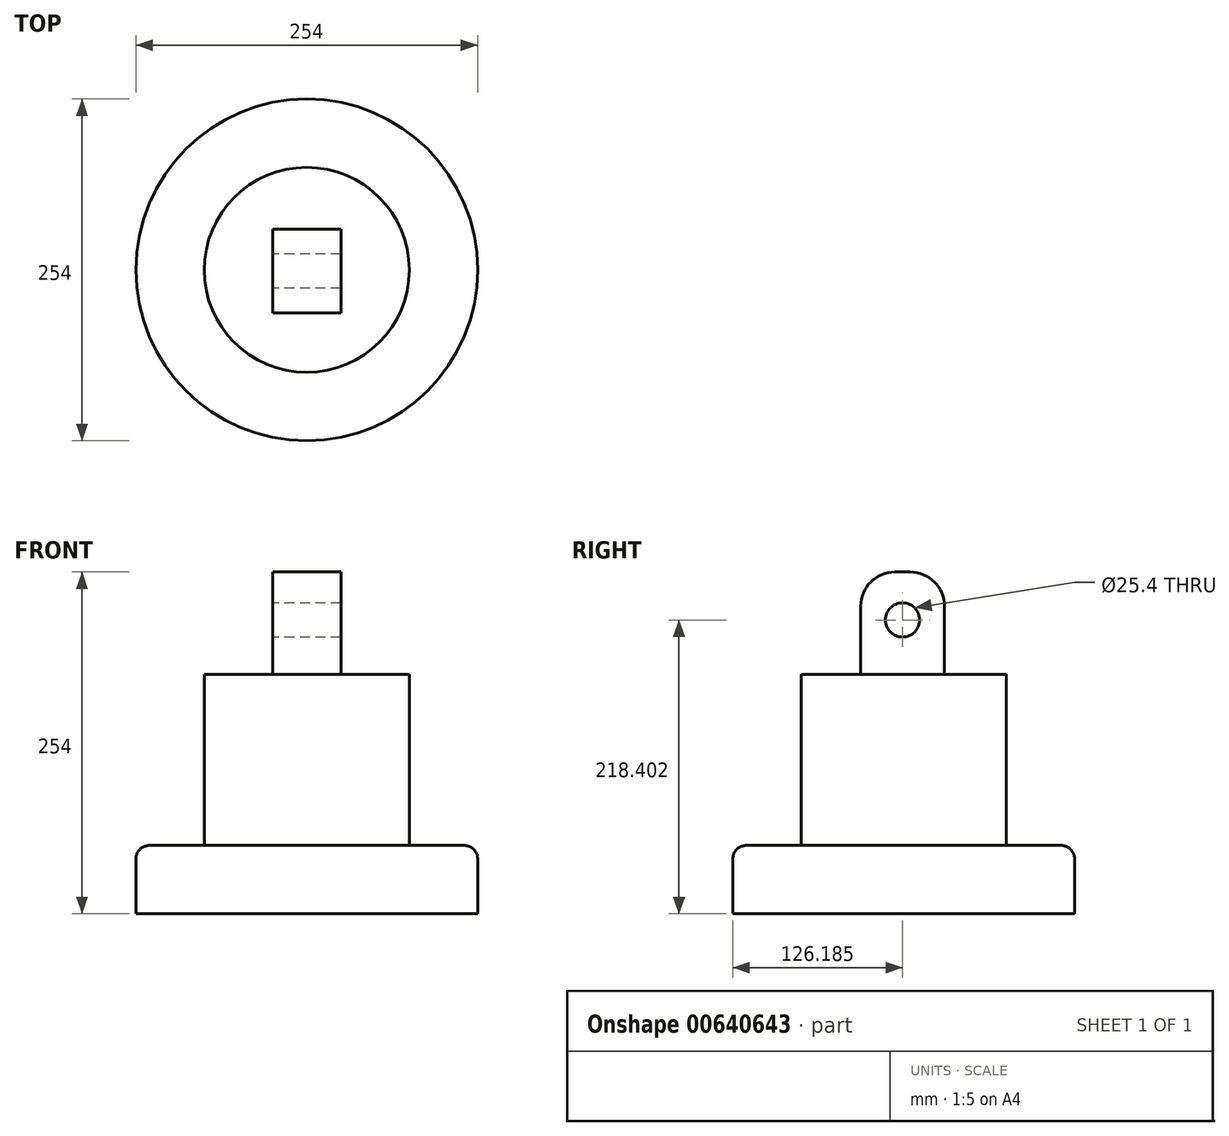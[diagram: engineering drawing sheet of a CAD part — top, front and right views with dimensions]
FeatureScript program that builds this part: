
annotation { "Feature Type Name" : "Feature", "Feature Type Description" : "" }
export const myFeature = defineFeature(function(context is Context, id is Id, definition is map)
    precondition{}
    {
        {
            var Q0;
            Q0=qCreatedBy(makeId("Front.planeOp"),FACE);
            var sketch = newSketch(context, id + "F0", { "sketchPlane" : qUnion([Q0])});
            skLineSegment(sketch, "E0", {"start": v(-155.87, 46) * mm, "end": v(-155.87, -4.8) * mm});
            skLineSegment(sketch, "E1", {"start": v(-155.87, -4.8) * mm, "end": v(-28.87, -4.8) * mm});
            skLineSegment(sketch, "E2", {"start": v(-28.87, -4.8) * mm, "end": v(-28.87, 46) * mm});
            skLineSegment(sketch, "E3", {"start": v(-28.87, 46) * mm, "end": v(-155.87, 46) * mm});
            skSolve(sketch);
        }
        {
            var Q0;
            Q0=makeQuery(id+"F0.imprint","IMPRINT",FACE,{"disambiguationData":[TD([[makeQuery(id+"F0.imprint","IMPRINT",EDGE,{"derivedFrom":sQuery(id+"F0.wireOp",EDGE,"E0")}),1.0]])]});
            var Q1;
            Q1=sQuery(id+"F0.wireOp",EDGE,"E0");
            revolve(context, id + "F1", {"entities" : qUnion([Q0]), "axis" : qUnion([Q1]), "revolveType" : RevolveType.FULL});
        }
        {
            var Q0;
            Q0=makeQuery(id+"F1.opRevolve","SWEPT_FACE",FACE,{"disambiguationData":[OSD([sQuery(id+"F0.wireOp",EDGE,"E3")])]});
            var sketch = newSketch(context, id + "F2", { "sketchPlane" : qUnion([Q0])});
            skCircle(sketch, "E4", {"center": v(-155.87, 0) * mm, "radius": 76.2 * mm});
            skSolve(sketch);
        }
        {
            var Q0;
            Q0=qSketchRegion(id+"F2",true);
            extrude(context, id + "F3", {"entities" : qUnion([Q0]), "operationType" : NewBodyOperationType.ADD, "depth" : 127 * mm});
        }
        {
            var Q0;
            Q0=makeQuery(id+"F3.opExtrude","CAP_FACE",FACE,{"disambiguationData":[OSD([sQuery(id+"F2.wireOp",EDGE,"E4")])],"isStart":false});
            var sketch = newSketch(context, id + "F4", { "sketchPlane" : qUnion([Q0])});
            skLineSegment(sketch, "E5", {"start": v(-155.87, 30.3) * mm, "end": v(-130.47, 30.3) * mm});
            skLineSegment(sketch, "E6", {"start": v(-130.47, 30.3) * mm, "end": v(-130.47, -31.94) * mm});
            skLineSegment(sketch, "E7", {"start": v(-130.47, -31.94) * mm, "end": v(-155.87, -31.94) * mm});
            skLineSegment(sketch, "E8", {"start": v(-155.87, 30.3) * mm, "end": v(-181.27, 30.3) * mm});
            skLineSegment(sketch, "E9", {"start": v(-181.27, 30.3) * mm, "end": v(-181.27, -31.94) * mm});
            skLineSegment(sketch, "E10", {"start": v(-181.27, -31.94) * mm, "end": v(-155.87, -31.94) * mm});
            skPoint(sketch, "E11.start.orphan", {"position": v(-155.87, 0) * mm});
            skSolve(sketch);
        }
        {
            var Q0;
            Q0=makeQuery(id+"F4.imprint","IMPRINT",FACE,{"disambiguationData":[TD([[makeQuery(id+"F4.imprint","IMPRINT",EDGE,{"derivedFrom":sQuery(id+"F4.wireOp",EDGE,"E5")}),-1.0]])]});
            extrude(context, id + "F5", {"entities" : qUnion([Q0]), "operationType" : NewBodyOperationType.ADD, "depth" : 76.2 * mm});
        }
        {
            var Q0;
            Q0=makeQuery(id+"F5.opExtrude","CAP_EDGE",EDGE,{"disambiguationData":[OSD([sQuery(id+"F4.wireOp",EDGE,"E5"),sQuery(id+"F4.wireOp",EDGE,"E8")])],"isStart":false});
            fillet(context, id + "F6", {"entities" : qUnion([Q0]), "radius" : 25.4 * mm, "tangentPropagation" : true, "allowEdgeOverflow" : false});
        }
        {
            var Q0;
            Q0=makeQuery(id+"F5.opExtrude","CAP_EDGE",EDGE,{"disambiguationData":[OSD([sQuery(id+"F4.wireOp",EDGE,"E7"),sQuery(id+"F4.wireOp",EDGE,"E10")])],"isStart":false});
            fillet(context, id + "F7", {"entities" : qUnion([Q0]), "radius" : 25.4 * mm, "tangentPropagation" : true, "allowEdgeOverflow" : false});
        }
        {
            var Q0;
            Q0=makeQuery(id+"F5.opExtrude","SWEPT_FACE",FACE,{"disambiguationData":[OSD([sQuery(id+"F4.wireOp",EDGE,"E9")])]});
            var sketch = newSketch(context, id + "F8", { "sketchPlane" : qUnion([Q0])});
            skCircle(sketch, "E12", {"center": v(0.81, 213.61) * mm, "radius": 12.7 * mm});
            skSolve(sketch);
        }
        {
            var Q0;
            Q0=makeQuery(id+"F1.opRevolve","SWEPT_FACE",FACE,{"disambiguationData":[OSD([sQuery(id+"F0.wireOp",EDGE,"E1")])]});
            var sketch = newSketch(context, id + "F9", { "sketchPlane" : qUnion([Q0])});
            skCircle(sketch, "E13", {"center": v(-155.87, 0) * mm, "radius": 19.05 * mm});
            skSolve(sketch);
        }
        {
            var Q0;
            Q0=makeQuery(id+"F8.imprint","IMPRINT",FACE,{"disambiguationData":[TD([[makeQuery(id+"F8.imprint","IMPRINT",EDGE,{"derivedFrom":sQuery(id+"F8.wireOp",EDGE,"E12")}),1.0]])]});
            extrude(context, id + "F10", {"entities" : qUnion([Q0]), "operationType" : NewBodyOperationType.REMOVE, "endBound" : BoundingType.THROUGH_ALL, "oppositeDirection" : true, "depth" : 25.4 * mm});
        }
        {
            var Q0;
            Q0=makeQuery(id+"F1.opRevolve","SWEPT_EDGE",EDGE,{"disambiguationData":[OSD([sQuery(id+"F0.wireOp",EDGE,"E2"),sQuery(id+"F0.wireOp",EDGE,"E3")])]});
            fillet(context, id + "F11", {"entities" : qUnion([Q0]), "radius" : 10 * mm, "tangentPropagation" : true, "allowEdgeOverflow" : false});
        }
    });
